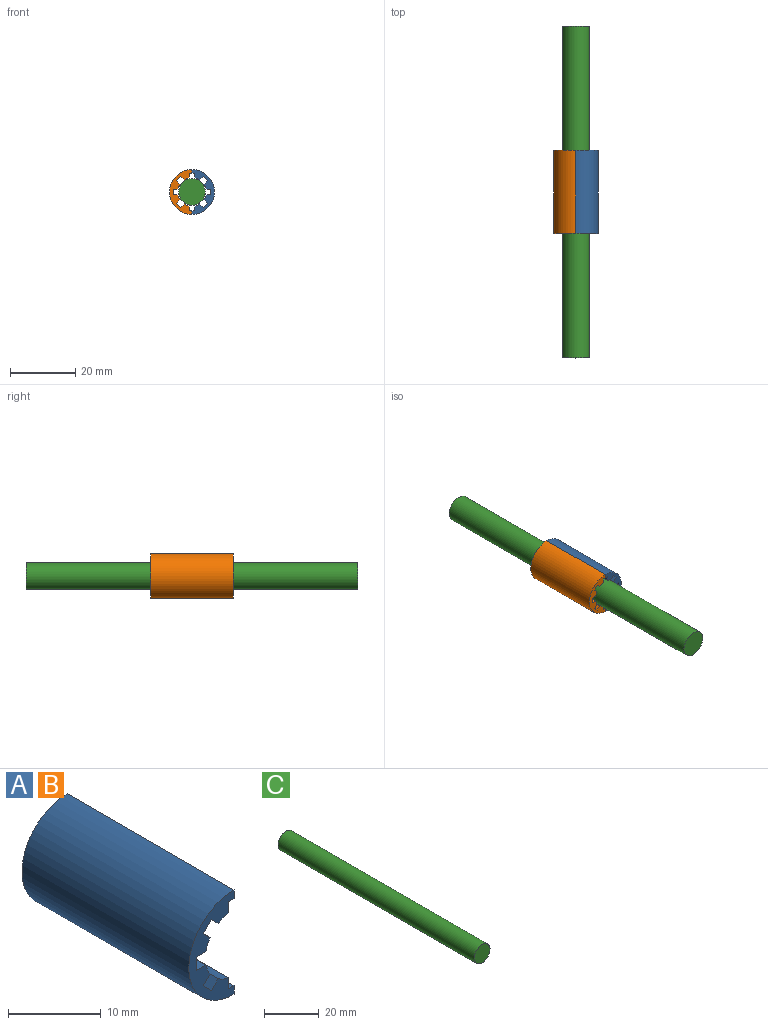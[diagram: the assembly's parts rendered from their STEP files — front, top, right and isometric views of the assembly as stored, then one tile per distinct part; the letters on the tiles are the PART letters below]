
ASSEMBLY  parts=3 mates=3
PART A: 22 faces, bbox 6.9x25.4x13.8 mm
  f0: cylinder r=6.88mm len=25.4mm, axis (0,1,0), area 548.8mm2, adj f13,f14,f20,f21
  f1: cylinder r=4.36mm len=25.4mm, axis (0,1,0), area 42.3mm2, adj f2,f7,f13,f14
  f2: plane 25.4x1.04mm, normal (0.71,0,0.71), area 37.2mm2, adj f1,f4,f13,f14
  f3: plane 25.4x1.04mm, normal (-0.71,0,-0.71), area 37.2mm2, adj f4,f13,f14,f15
  f4: plane 25.4x1.24mm, normal (0.71,0,-0.71), area 44.5mm2, adj f2,f3,f13,f14
  f5: cylinder r=4.36mm len=25.4mm, axis (0,1,0), area 42.3mm2, adj f6,f11,f13,f14
  f6: plane 25.4x1.46mm, normal (0,0,1), area 37.2mm2, adj f5,f8,f13,f14
  f7: plane 25.4x1.46mm, normal (0,0,-1), area 37.2mm2, adj f1,f8,f13,f14
  f8: plane 25.4x1.75mm, normal (1,0,0), area 44.5mm2, adj f6,f7,f13,f14
  f9: cylinder r=4.36mm len=25.4mm, axis (0,1,0), area 42.3mm2, adj f10,f13,f14,f17
  f10: plane 25.4x1.04mm, normal (-0.71,0,0.71), area 37.2mm2, adj f9,f12,f13,f14
  f11: plane 25.4x1.04mm, normal (0.71,0,-0.71), area 37.2mm2, adj f5,f12,f13,f14
  f12: plane 25.4x1.24mm, normal (0.71,0,0.71), area 44.5mm2, adj f10,f11,f13,f14
  f13: plane 13.75x6.88mm, normal (0,-1,0), area 34.5mm2, adj f0,f1,f2,f3,f4,f5,f6,f7
  f14: plane 13.75x6.88mm, normal (0,1,0), area 34.5mm2, adj f0,f1,f2,f3,f4,f5,f6,f7
  f15: cylinder r=4.36mm len=25.4mm, axis (0,1,0), area 42.3mm2, adj f3,f13,f14,f19
  f16: plane 25.4x0.88mm, normal (0,0,1), area 22.3mm2, adj f13,f14,f17,f21
  f17: plane 25.4x1.46mm, normal (1,0,0), area 37.2mm2, adj f9,f13,f14,f16
  f18: plane 25.4x0.88mm, normal (0,0,-1), area 22.3mm2, adj f13,f14,f19,f20
  f19: plane 25.4x1.46mm, normal (1,0,0), area 37.2mm2, adj f13,f14,f15,f18
  f20: plane 25.4x1.14mm, normal (1,0,0), area 28.9mm2, adj f0,f13,f14,f18
  f21: plane 25.4x1.14mm, normal (1,0,0), area 28.9mm2, adj f0,f13,f14,f16
PART B: same geometry as A
PART C: 3 faces, bbox 8.1x101.6x8.1 mm
  f0: plane 8.14x8.14mm, normal (0,-1,0), area 52mm2, adj f2
  f1: plane 8.14x8.14mm, normal (0,1,0), area 52mm2, adj f2
  f2: cylinder r=4.07mm len=101.6mm, axis (0,-1,0), area 2598.4mm2, adj f0,f1
PLACE A rot(axis=(0,1,0),180deg) t=(0,0,0)mm
PLACE B at identity
PLACE C at identity
MATE revolute A.f0 <-> C.f2  axis (0,1,0) through (0,0,0)mm
MATE slider B.f0 <-> C.f2  axis (0,1,0) through (0,0,0)mm
MATE planar B.f13 <-> A.f13  axis (0,-1,0) through (0,-12.7,6.88)mm
